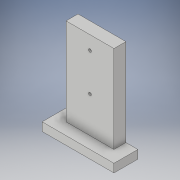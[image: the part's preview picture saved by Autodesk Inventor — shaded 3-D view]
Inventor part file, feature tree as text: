
AUTODESK INVENTOR PART (.ipt)
format: ipt  version: 2017 (Build 210142000, 142)  size: 122,880 bytes
history: native  units: in
note: dims shown in document units (in); Inventor stores cm internally (conversion verified against a paired STEP export)
features: extrude x2, sketch x2
ambient origin geometry x8: Origin, YZ Plane, XZ Plane, XY Plane, X Axis, Y Axis, Z Axis, Center Point
bodies: Solid1 (feature_tree)
feature tree (4):
  extrude  "Extrusion1"  Depth=1.575in
  extrude  "Extrusion3"  Depth=0.5in
  sketch  "Sketch1"  dims[d0=1.575in d1=0.6in]
  sketch  "Sketch3"  dims[d2=2.4in d3=0.122in d4=0.122in d5=0.57in d6=1.0in d7=1.0in d8=4.0in d9=0.5in d10=0.5in d11=0.35in d12=0.5in d13=0.0in d16=0.5in d17=0.0in]
